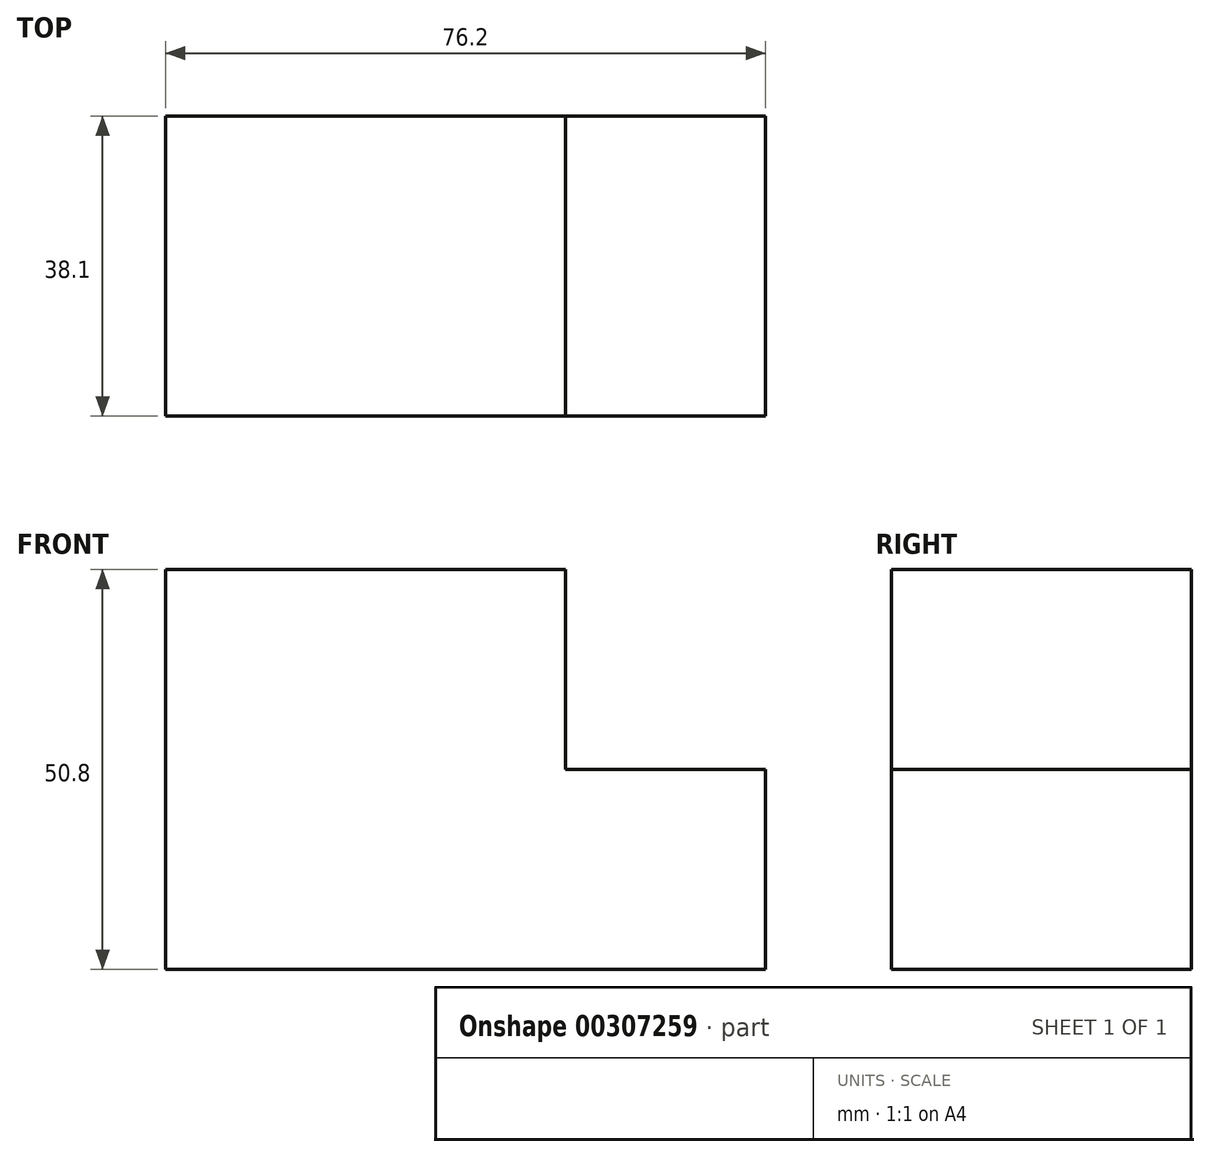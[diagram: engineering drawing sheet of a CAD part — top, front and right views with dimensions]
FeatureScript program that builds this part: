
annotation { "Feature Type Name" : "Feature", "Feature Type Description" : "" }
export const myFeature = defineFeature(function(context is Context, id is Id, definition is map)
    precondition{}
    {
        {
            var Q0;
            Q0=qCreatedBy(makeId("Front.planeOp"),FACE);
            var sketch = newSketch(context, id + "F0", { "sketchPlane" : qUnion([Q0])});
            skLineSegment(sketch, "E0", {"start": v(-40.2, -39.08) * mm, "end": v(36, -39.08) * mm});
            skLineSegment(sketch, "E1", {"start": v(36, -39.08) * mm, "end": v(36, -13.68) * mm});
            skLineSegment(sketch, "E2", {"start": v(36, -13.68) * mm, "end": v(10.6, -13.68) * mm});
            skLineSegment(sketch, "E3", {"start": v(10.6, -13.68) * mm, "end": v(10.6, 11.72) * mm});
            skLineSegment(sketch, "E4", {"start": v(10.6, 11.72) * mm, "end": v(-40.2, 11.72) * mm});
            skLineSegment(sketch, "E5", {"start": v(-40.2, 11.72) * mm, "end": v(-40.2, -39.08) * mm});
            skSolve(sketch);
        }
        {
            var Q0;
            Q0=makeQuery(id+"F0.imprint","IMPRINT",FACE,{"disambiguationData":[TD([[makeQuery(id+"F0.imprint","IMPRINT",EDGE,{"derivedFrom":sQuery(id+"F0.wireOp",EDGE,"E0")}),1.0]])]});
            extrude(context, id + "F1", {"entities" : qUnion([Q0]), "depth" : 38.1 * mm});
        }
    });
